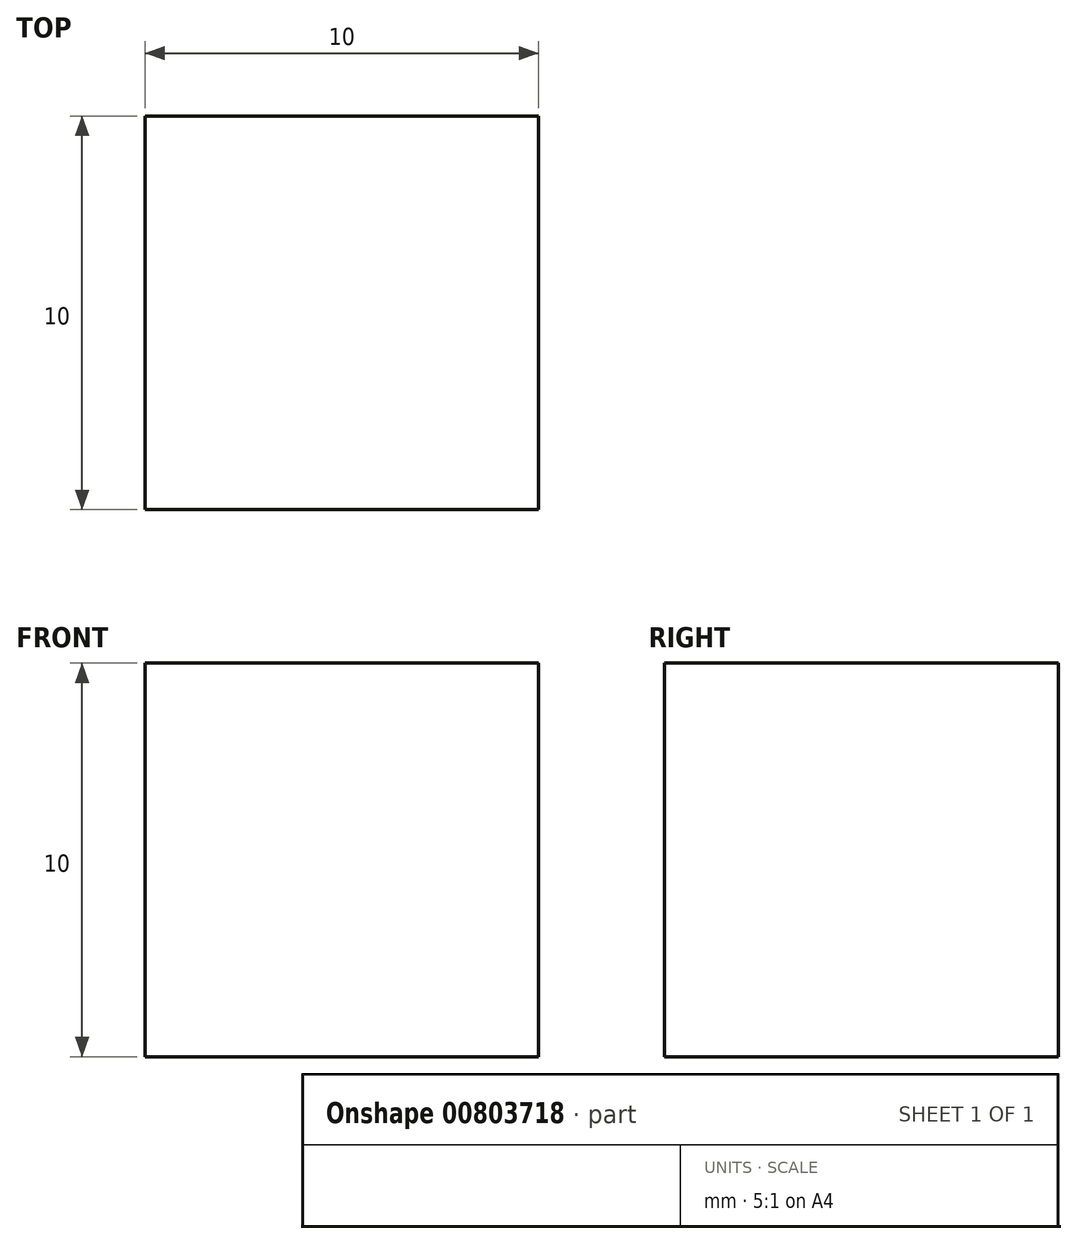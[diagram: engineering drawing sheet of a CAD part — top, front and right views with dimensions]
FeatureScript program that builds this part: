
annotation { "Feature Type Name" : "Feature", "Feature Type Description" : "" }
export const myFeature = defineFeature(function(context is Context, id is Id, definition is map)
    precondition{}
    {
        {
            var Q0;
            Q0=qCreatedBy(makeId("Top.planeOp"),FACE);
            var sketch = newSketch(context, id + "F0", { "sketchPlane" : qUnion([Q0])});
            skLineSegment(sketch, "E0.bottom", {"start": v(0, 0) * mm, "end": v(10, 0) * mm});
            skLineSegment(sketch, "E0.top", {"start": v(0, 10) * mm, "end": v(10, 10) * mm});
            skLineSegment(sketch, "E0.left", {"start": v(0, 0) * mm, "end": v(0, 10) * mm});
            skLineSegment(sketch, "E0.right", {"start": v(10, 0) * mm, "end": v(10, 10) * mm});
            skLineSegment(sketch, "E1.left", {"start": v(0, 0) * mm, "end": v(0, -1) * mm});
            skSolve(sketch);
        }
        {
            var Q0;
            Q0=makeQuery(id+"F0.imprint","IMPRINT",FACE,{"disambiguationData":[TD([[makeQuery(id+"F0.imprint","IMPRINT",EDGE,{"derivedFrom":sQuery(id+"F0.wireOp",EDGE,"E0.top")}),-1.0]])]});
            var Q1;
            Q1=makeQuery(id+"F0.imprint","IMPRINT",FACE,{"disambiguationData":[TD([[makeQuery(id+"F0.imprint","IMPRINT",EDGE,{"derivedFrom":sQuery(id+"F0.wireOp",EDGE,"KYz3I5JV-po3z-2gd2-2yHW-CX9zJ0YFtxDT.top")}),-1.0]])]});
            var Q2;
            Q2=makeQuery(id+"F0.imprint","IMPRINT",FACE,{"disambiguationData":[TD([[makeQuery(id+"F0.imprint","IMPRINT",EDGE,{"derivedFrom":sQuery(id+"F0.wireOp",EDGE,"3xrTa0RX-hzoA-z3Dr-MIwN-Q0MkDwxUOKV7.top")}),-1.0]])]});
            var Q3;
            Q3=makeQuery(id+"F0.imprint","IMPRINT",FACE,{"disambiguationData":[TD([[makeQuery(id+"F0.imprint","IMPRINT",EDGE,{"derivedFrom":sQuery(id+"F0.wireOp",EDGE,"gMvkpBWy-B4q9-d7K8-avPd-zKeyMb6xpmFd.top")}),-1.0]])]});
            extrude(context, id + "F1", {"entities" : qUnion([Q0, Q1, Q2, Q3]), "depth" : 10 * mm, "offsetDistance" : 25 * mm});
        }
    });
